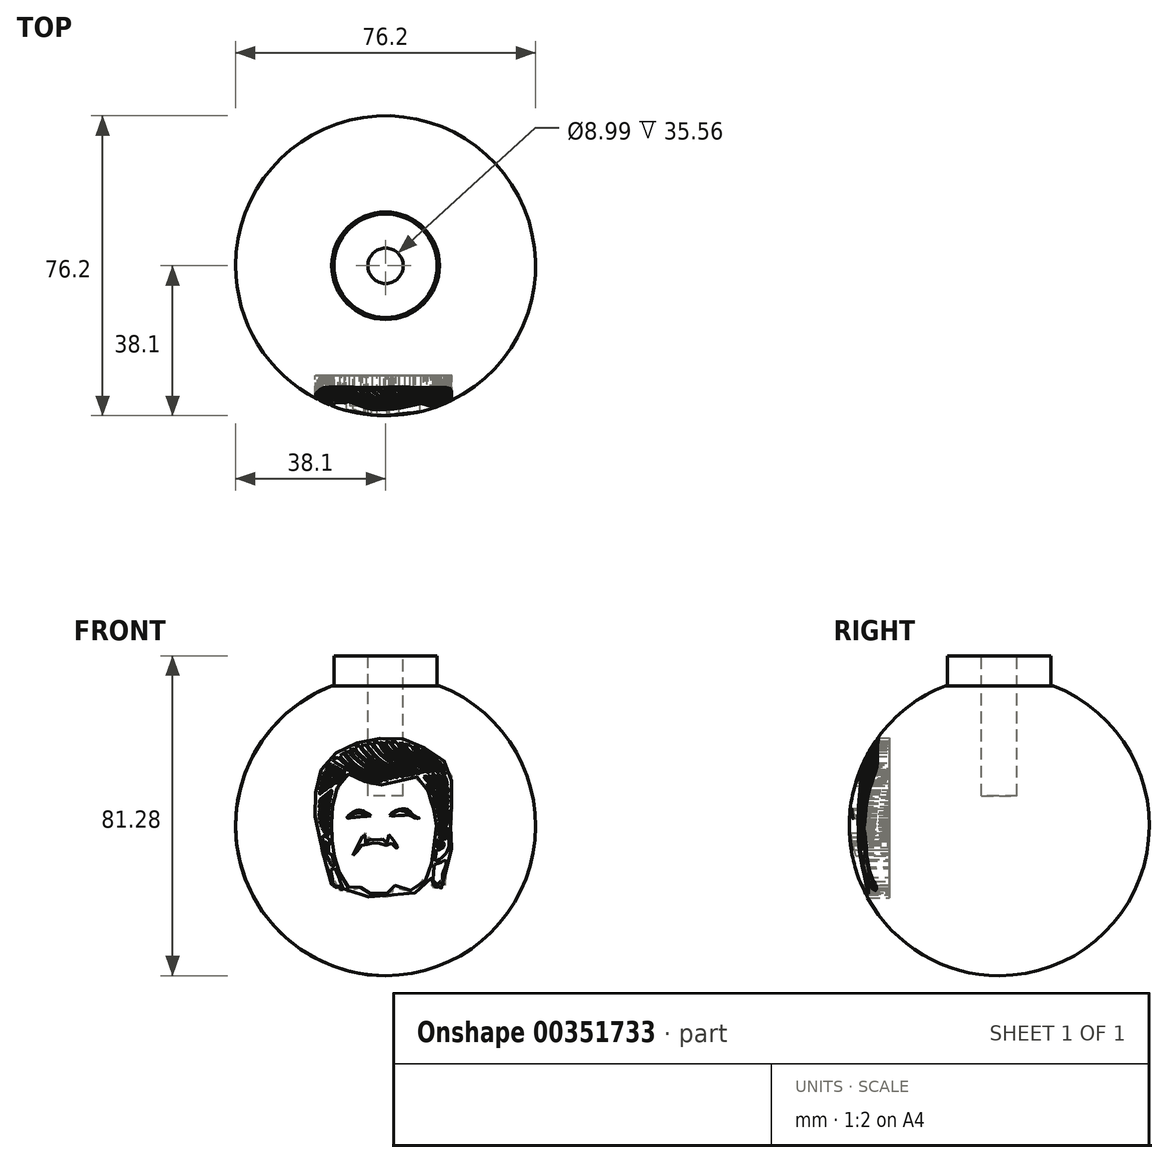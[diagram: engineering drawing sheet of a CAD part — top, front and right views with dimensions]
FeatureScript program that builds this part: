
annotation { "Feature Type Name" : "Feature", "Feature Type Description" : "" }
export const myFeature = defineFeature(function(context is Context, id is Id, definition is map)
    precondition{}
    {
        {
            var Q0;
            Q0=qCreatedBy(makeId("Front.planeOp"),FACE);
            var sketch = newSketch(context, id + "F0", { "sketchPlane" : qUnion([Q0])});
            skArc(sketch, "E0", {"start": v(0, 38.1) * mm, "mid": v(-38.1, 0) * mm, "end": v(0, -38.1) * mm});
            skLineSegment(sketch, "E1", {"start": v(0, 38.1) * mm, "end": v(0, -38.1) * mm});
            skSolve(sketch);
        }
        {
            var Q0;
            Q0=makeQuery(id+"F0.imprint","IMPRINT",FACE,{"disambiguationData":[TD([[makeQuery(id+"F0.imprint","IMPRINT",EDGE,{"derivedFrom":sQuery(id+"F0.wireOp",EDGE,"E0")}),1.0]])]});
            var Q1;
            Q1=sQuery(id+"F0.wireOp",EDGE,"E0");
            var Q2;
            Q2=sQuery(id+"F0.wireOp",EDGE,"E1");
            revolve(context, id + "F1", {"entities" : qUnion([Q0]), "surfaceEntities" : qUnion([Q1]), "axis" : qUnion([Q2]), "revolveType" : RevolveType.FULL});
        }
        {
            var Q0;
            Q0=qCreatedBy(makeId("Top.planeOp"),FACE);
            cPlane(context, id + "F2", {"entities" : qUnion([Q0]), "cplaneType" : CPlaneType.OFFSET, "offset" : 35.56 * mm, "width" : 152.4 * mm, "height" : 152.4 * mm});
        }
        {
            var Q0;
            Q0=qCreatedBy(id+"F2.planeOp",FACE);
            var sketch = newSketch(context, id + "F3", { "sketchPlane" : qUnion([Q0])});
            skLineSegment(sketch, "E2.bottom", {"start": v(16.51, 16.51) * mm, "end": v(-16.51, 16.51) * mm});
            skLineSegment(sketch, "E2.top", {"start": v(16.51, -16.51) * mm, "end": v(-16.51, -16.51) * mm});
            skLineSegment(sketch, "E2.left", {"start": v(16.51, 16.51) * mm, "end": v(16.51, -16.51) * mm});
            skLineSegment(sketch, "E2.right", {"start": v(-16.51, 16.51) * mm, "end": v(-16.51, -16.51) * mm});
            skPoint(sketch, "E2.middle", {"position": v(0, 0) * mm});
            skSolve(sketch);
        }
        {
            var Q0;
            Q0=makeQuery(id+"F3.imprint","IMPRINT",FACE,{"disambiguationData":[TD([[makeQuery(id+"F3.imprint","IMPRINT",EDGE,{"derivedFrom":sQuery(id+"F3.wireOp",EDGE,"E2.bottom")}),1.0]])]});
            extrude(context, id + "F4", {"entities" : qUnion([Q0]), "operationType" : NewBodyOperationType.REMOVE, "depth" : 25.4 * mm});
        }
        {
            var Q0;
            Q0=qCreatedBy(makeId("Front.planeOp"),FACE);
            cPlane(context, id + "F5", {"entities" : qUnion([Q0]), "cplaneType" : CPlaneType.OFFSET, "offset" : 40.64 * mm, "width" : 152.4 * mm, "height" : 152.4 * mm});
        }
        {
            var Q0;
            Q0=qCreatedBy(id+"F5.planeOp",FACE);
            var sketch = newSketch(context, id + "F6", { "sketchPlane" : qUnion([Q0])});
            skFitSpline(sketch, "E3", {"points": [v(-13.42, 4.94) * mm, v(-13.77, 1.48) * mm, v(-13.69, -2.98) * mm, v(-12.93, -8.07) * mm, v(-10.73, -14.01) * mm, v(-8.94, -16.04) * mm, v(-7.44, -16.48) * mm, v(-6.43, -16.38) * mm, v(-6.53, -16.1) * mm, v(-6.53, -15.75) * mm, v(-6.33, -15.56) * mm, v(-6.1, -15.27) * mm, v(-5.85, -15.13) * mm, v(-5.9, -15.51) * mm, v(-6.04, -15.75) * mm, v(-6.04, -16.04) * mm, v(-5.9, -16.38) * mm, v(-5.7, -16.62) * mm, v(-4.17, -17.17) * mm, v(-3.17, -17.46) * mm, v(-1.74, -17.5) * mm, v(0.28, -17.23) * mm, v(1.86, -16.73) * mm, v(2.44, -16.33) * mm, v(2.69, -15.98) * mm, v(2.14, -15.38) * mm, v(1.9, -15.13) * mm, v(1.9, -15.09) * mm, v(2.03, -15.13) * mm, v(2.29, -15.16) * mm, v(2.64, -15.3) * mm, v(2.9, -15.65) * mm, v(3.03, -16.11) * mm, v(3.36, -16.11) * mm, v(3.95, -16.24) * mm, v(4.51, -16.34) * mm, v(5.17, -16.44) * mm, v(5.99, -16.5) * mm, v(8.28, -15.87) * mm, v(11.23, -11.44) * mm, v(12.37, -4.65) * mm, v(12.9, 0) * mm, v(10.78, 8.79) * mm, v(8.61, 12.24) * mm, v(7.1, 12.14) * mm, v(-0.99, 10.36) * mm, v(-1.74, 10.17) * mm, v(-3.25, 10.26) * mm, v(-9.18, 13.18) * mm, v(-9.74, 12.43) * mm, v(-11.15, 10.54) * mm, v(-12.1, 9.98) * mm, v(-13.42, 4.94) * mm]});
            skFitSpline(sketch, "E4", {"points": [v(-16.44, 14.23) * mm, v(-15.15, 16.37) * mm, v(-10.88, 19.62) * mm, v(-5.66, 21.5) * mm, v(1.82, 22.36) * mm, v(7.43, 21.07) * mm, v(14.77, 16.6) * mm, v(16.5, 14.16) * mm, v(16.78, 11.72) * mm, v(16.78, 5.82) * mm, v(16.64, 0) * mm, v(16.45, 0) * mm, v(16.55, -1.09) * mm, v(16.86, -5.2) * mm, v(16.04, -7.5) * mm, v(15.94, -8.77) * mm, v(15.64, -10.4) * mm, v(15.19, -12.44) * mm, v(15.33, -14.6) * mm, v(15.33, -15.53) * mm, v(14.8, -16.07) * mm, v(13.82, -15.82) * mm, v(13.86, -16.43) * mm, v(12.35, -15.82) * mm, v(11.4, -15) * mm, v(11.59, -13.12) * mm, v(10.4, -14.85) * mm, v(6.34, -17.33) * mm, v(3.46, -17.05) * mm, v(2.34, -17.15) * mm, v(0.83, -18.05) * mm, v(-2.12, -18.34) * mm, v(-4.5, -17.98) * mm, v(-5.8, -17.11) * mm, v(-6.76, -17.17) * mm, v(-8.1, -17.26) * mm, v(-10.36, -16.11) * mm, v(-10.1, -17) * mm, v(-11.45, -16.63) * mm, v(-13.57, -15.24) * mm, v(-14.3, -10.82) * mm, v(-14.67, -10.07) * mm, v(-15.84, -8.34) * mm, v(-16.3, -6.15) * mm, v(-16.8, -1.78) * mm, v(-16.96, -0.91) * mm, v(-17.72, 1.07) * mm, v(-17.82, 3.82) * mm, v(-17.57, 6.16) * mm, v(-17.26, 6.77) * mm, v(-17.62, 7.48) * mm, v(-17.35, 11.15) * mm, v(-16.44, 14.23) * mm]});
            skFitSpline(sketch, "E5", {"points": [v(-16.9, 7.74) * mm, v(-16.92, 9.4) * mm, v(-16.35, 11.89) * mm, v(-15.38, 14.34) * mm, v(-14.2, 16.09) * mm, v(-13.85, 15.83) * mm, v(-13.44, 15.63) * mm, v(-9.88, 13.7) * mm, v(-9.85, 13.55) * mm, v(-9.94, 13.25) * mm, v(-9.96, 13.07) * mm, v(-10.02, 12.86) * mm, v(-10.1, 12.72) * mm, v(-10.26, 12.56) * mm, v(-10.4, 12.35) * mm, v(-11.15, 11.44) * mm, v(-11.38, 11.08) * mm, v(-12.27, 10.73) * mm, v(-12.68, 10.65) * mm, v(-13.14, 10.5) * mm, v(-13.39, 10.27) * mm, v(-13.8, 10.01) * mm, v(-15, 9.18) * mm, v(-16.54, 7.9) * mm, v(-16.71, 7.77) * mm, v(-16.9, 7.74) * mm]});
            skFitSpline(sketch, "E6", {"points": [v(-13.42, 9.18) * mm, v(-13.42, 8.8) * mm, v(-13.42, 8.66) * mm, v(-13.62, 7.7) * mm, v(-13.8, 6.07) * mm, v(-13.94, 4.94) * mm, v(-14.2, 2.5) * mm, v(-14.2, 0.72) * mm, v(-14.2, -2.59) * mm, v(-14.2, -2.74) * mm, v(-14.45, -2.56) * mm, v(-15.6, -1.9) * mm, v(-16.1, -1.17) * mm, v(-16.54, 0) * mm, v(-16.99, 1.6) * mm, v(-17.12, 3.67) * mm, v(-16.96, 5.93) * mm, v(-16.79, 6.52) * mm, v(-13.8, 9.18) * mm, v(-13.39, 9.38) * mm, v(-13.42, 9.18) * mm]});
            skFitSpline(sketch, "E7", {"points": [v(-13.8, -11.08) * mm, v(-13.6, -12.82) * mm, v(-13.42, -14.46) * mm, v(-13.05, -15.35) * mm, v(-12.64, -15.75) * mm, v(-12.36, -15.64) * mm, v(-12.1, -15.36) * mm, v(-11.92, -15.21) * mm, v(-11.45, -15.75) * mm, v(-11.45, -16.16) * mm, v(-11.15, -16.16) * mm, v(-10.8, -16.27) * mm, v(-10.82, -15.75) * mm, v(-11.15, -15.16) * mm, v(-11.89, -12.97) * mm, v(-12.38, -11.86) * mm, v(-12.85, -10.98) * mm, v(-13.23, -10.9) * mm, v(-13.39, -10.96) * mm, v(-13.8, -11.08) * mm]});
            skFitSpline(sketch, "E8", {"points": [v(-13.16, -10.5) * mm, v(-13.8, -9.94) * mm, v(-14.2, -9.49) * mm, v(-14.2, -9.05) * mm, v(-15, -7.55) * mm, v(-15, -5.02) * mm, v(-15, -4) * mm, v(-15.18, -4.12) * mm, v(-15.42, -4.98) * mm, v(-15.58, -6.15) * mm, v(-15.7, -5.07) * mm, v(-15.78, -4.1) * mm, v(-15.96, -2.43) * mm, v(-15.26, -2.64) * mm, v(-15, -2.98) * mm, v(-14.2, -3.34) * mm, v(-14.27, -3.64) * mm, v(-14.38, -4.38) * mm, v(-14.5, -5.67) * mm, v(-14.54, -6.55) * mm, v(-14.37, -7.35) * mm, v(-14.07, -7.15) * mm, v(-13.8, -6.9) * mm, v(-13.39, -8.16) * mm, v(-13.06, -9.97) * mm, v(-13.16, -10.5) * mm]});
            skFitSpline(sketch, "E9", {"points": [v(13.42, -6.15) * mm, v(12.99, -6.15) * mm, v(12.86, -6.8) * mm, v(12.82, -7.61) * mm, v(12.56, -8.85) * mm, v(12.77, -8.94) * mm, v(13.12, -8.85) * mm, v(14.19, -8.21) * mm, v(15.77, -6.15) * mm, v(16.15, -3.3) * mm, v(16.07, -2.82) * mm, v(15.43, -3.22) * mm, v(14.59, -3.52) * mm, v(14.04, -3.4) * mm, v(14.47, -3.88) * mm, v(14.77, -4.46) * mm, v(14.89, -5.2) * mm, v(14.28, -5.6) * mm, v(13.42, -6.15) * mm]});
            skFitSpline(sketch, "E10", {"points": [v(13.17, -3.55) * mm, v(13.14, -4.25) * mm, v(13.07, -5.2) * mm, v(13.1, -5.52) * mm, v(14.01, -4.88) * mm, v(14.13, -4.52) * mm, v(13.17, -3.55) * mm]});
            skFitSpline(sketch, "E11", {"points": [v(15.68, -0.47) * mm, v(15.37, -0.58) * mm, v(14.33, -1.18) * mm, v(13.64, -1.54) * mm, v(13.86, -1.63) * mm, v(14.42, -1.64) * mm, v(15.05, -1.52) * mm, v(15.75, -1.14) * mm, v(15.82, -0.65) * mm, v(15.68, -0.47) * mm]});
            skFitSpline(sketch, "E12", {"points": [v(13.28, -1.9) * mm, v(13.48, -2.43) * mm, v(14.02, -2.43) * mm, v(14.7, -2.38) * mm, v(15.2, -2.22) * mm, v(15.73, -1.91) * mm, v(16, -1.79) * mm, v(15.96, -1.4) * mm, v(15.87, -1.4) * mm, v(15.2, -1.84) * mm, v(14.61, -1.95) * mm, v(13.9, -1.91) * mm, v(13.28, -1.9) * mm]});
            skFitSpline(sketch, "E13", {"points": [v(13.54, -2.76) * mm, v(13.8, -3.08) * mm, v(14.04, -3.17) * mm, v(14.56, -3.15) * mm, v(15.06, -3.01) * mm, v(15.53, -2.83) * mm, v(15.87, -2.7) * mm, v(16.05, -2.52) * mm, v(16.02, -2.13) * mm, v(15.9, -2.16) * mm, v(15.59, -2.36) * mm, v(15.06, -2.6) * mm, v(14.7, -2.72) * mm, v(14.06, -2.76) * mm, v(13.54, -2.76) * mm]});
            skFitSpline(sketch, "E14", {"points": [v(-4.92, -10.15) * mm, v(-4.48, -10.38) * mm, v(-3.3, -10.82) * mm, v(-3.46, -10.96) * mm, v(-4.93, -11.44) * mm, v(-5.88, -12) * mm, v(-5.34, -11.95) * mm, v(-4.06, -11.53) * mm, v(-3.04, -11.25) * mm, v(-1.97, -11.1) * mm, v(-0.26, -11.1) * mm, v(0.76, -11.26) * mm, v(2.88, -11.68) * mm, v(3.83, -11.89) * mm, v(1.06, -10.7) * mm, v(0.14, -10.55) * mm, v(0.44, -10.34) * mm, v(0.9, -9.7) * mm, v(0.6, -9.81) * mm, v(-0.38, -10.1) * mm, v(-3.12, -10.27) * mm, v(-4.92, -10.15) * mm]});
            skFitSpline(sketch, "E15", {"points": [v(-4.97, -8.6) * mm, v(-3.92, -7.6) * mm, v(-3.47, -7.35) * mm, v(-3.1, -7.43) * mm, v(-2.85, -7.6) * mm, v(-2.12, -7.67) * mm, v(-1.56, -7.6) * mm, v(-1.22, -7.52) * mm, v(-0.93, -7.24) * mm, v(-0.75, -7.2) * mm, v(0, -7.6) * mm, v(0.43, -7.82) * mm, v(1.22, -8.35) * mm, v(0.19, -8.23) * mm, v(-0.93, -8.14) * mm, v(-3.29, -8.17) * mm, v(-4.65, -8.56) * mm, v(-4.97, -8.6) * mm]});
            skFitSpline(sketch, "E16", {"points": [v(-7.37, -10.48) * mm, v(-5.48, -8.8) * mm, v(-5.21, -8.67) * mm, v(-5.21, -8.4) * mm, v(-4.35, -7.64) * mm, v(-3.82, -7.17) * mm, v(-3.15, -7.06) * mm, v(-2.64, -7.33) * mm, v(-1.88, -7.3) * mm, v(-1.23, -7.08) * mm, v(-0.6, -6.91) * mm, v(0.6, -7.55) * mm, v(2, -8.6) * mm, v(2.8, -8.9) * mm, v(3.3, -9.12) * mm, v(3.52, -9.26) * mm, v(4.29, -10.53) * mm, v(3.8, -10.12) * mm, v(2.8, -9.4) * mm, v(1.75, -9.13) * mm, v(0.5, -8.9) * mm, v(-0.84, -8.74) * mm, v(-1.22, -8.67) * mm, v(-3.26, -8.7) * mm, v(-5.15, -9.24) * mm, v(-7, -10.33) * mm, v(-7.37, -10.48) * mm]});
            skFitSpline(sketch, "E17", {"points": [v(-8.24, -7.51) * mm, v(-5.15, -1.79) * mm, v(-5.36, -2.76) * mm, v(-5.4, -3.28) * mm, v(-5.03, -4.28) * mm, v(-4.45, -4.65) * mm, v(-4.48, -3.97) * mm, v(-4.42, -3.16) * mm, v(-4.4, -2.85) * mm, v(-3.7, -3.4) * mm, v(-3.06, -3.8) * mm, v(-2.12, -3.64) * mm, v(-1.13, -2.98) * mm, v(-0.34, -3.97) * mm, v(0, -4.65) * mm, v(0.63, -3.97) * mm, v(0.78, -2.88) * mm, v(0.48, -2.13) * mm, v(0.42, -1.79) * mm, v(3.41, -6.15) * mm, v(1.11, -4.28) * mm, v(0.96, -4.65) * mm, v(0, -4.94) * mm, v(-0.34, -4.65) * mm, v(-2.12, -4.37) * mm, v(-2.12, -4.22) * mm, v(-3.29, -4.34) * mm, v(-4.06, -4.88) * mm, v(-4.51, -4.88) * mm, v(-5.27, -4.34) * mm, v(-7.72, -7.21) * mm, v(-8.24, -7.51) * mm]});
            skFitSpline(sketch, "E18", {"points": [v(-13.49, 16.72) * mm, v(-7.3, 13.04) * mm, v(-4.42, 11.6) * mm, v(-2.35, 10.89) * mm, v(-1.73, 10.98) * mm, v(-1.45, 11.08) * mm, v(-2.26, 11.26) * mm, v(-3.32, 11.7) * mm, v(-7.28, 13.54) * mm, v(-10.87, 16.16) * mm, v(-12.15, 17.57) * mm, v(-12.19, 17.54) * mm, v(-13.17, 17) * mm, v(-13.49, 16.72) * mm]});
            skFitSpline(sketch, "E19", {"points": [v(-11.6, 17.91) * mm, v(-11.17, 17.23) * mm, v(-9.23, 15.39) * mm, v(-6.3, 13.48) * mm, v(-3.15, 12.03) * mm, v(-1.41, 11.42) * mm, v(-1.1, 11.3) * mm, v(-0.36, 11.34) * mm, v(-1.17, 11.61) * mm, v(-2.9, 12.3) * mm, v(-5.19, 13.48) * mm, v(-9.13, 16.4) * mm, v(-10.78, 18.55) * mm, v(-10.9, 18.52) * mm, v(-11.36, 18.18) * mm, v(-11.6, 17.91) * mm]});
            skFitSpline(sketch, "E20", {"points": [v(-10.36, 18.74) * mm, v(-9.94, 18.08) * mm, v(-8.47, 16.27) * mm, v(-5.8, 14.26) * mm, v(-2.2, 12.32) * mm, v(0, 11.56) * mm, v(0.62, 11.5) * mm, v(0.86, 11.69) * mm, v(0, 12.06) * mm, v(-1.07, 12.52) * mm, v(-4.28, 14.33) * mm, v(-7.1, 16.4) * mm, v(-9.57, 19.04) * mm, v(-9.6, 19.14) * mm, v(-9.82, 19.11) * mm, v(-10.36, 18.74) * mm]});
            skFitSpline(sketch, "E21", {"points": [v(-9.17, 19.38) * mm, v(-8.87, 19.04) * mm, v(-8.27, 18.06) * mm, v(-3.65, 14.33) * mm, v(-1.64, 13.2) * mm, v(0.55, 12.12) * mm, v(1.46, 11.93) * mm, v(2.15, 11.96) * mm, v(0.83, 12.62) * mm, v(-0.77, 13.5) * mm, v(-5.19, 16.47) * mm, v(-8.16, 19.46) * mm, v(-8.3, 19.76) * mm, v(-9.17, 19.38) * mm]});
            skFitSpline(sketch, "E22", {"points": [v(-7.8, 19.96) * mm, v(-6.32, 17.98) * mm, v(-3.4, 15.64) * mm, v(-0.35, 13.7) * mm, v(2.59, 12.12) * mm, v(2.75, 12.18) * mm, v(3.52, 12.29) * mm, v(2.64, 12.78) * mm, v(1.46, 13.33) * mm, v(-1.1, 14.9) * mm, v(-4, 17.07) * mm, v(-6.34, 19.76) * mm, v(-6.73, 20.42) * mm, v(-6.98, 20.34) * mm, v(-7.8, 19.96) * mm]});
            skFitSpline(sketch, "E23", {"points": [v(-6.18, 20.42) * mm, v(-4.91, 18.58) * mm, v(-2.85, 16.6) * mm, v(-0.63, 15.07) * mm, v(1.02, 14.02) * mm, v(2.94, 13.03) * mm, v(4.13, 12.4) * mm, v(4.98, 12.48) * mm, v(4.76, 12.65) * mm, v(2.34, 13.94) * mm, v(0.22, 15.29) * mm, v(-0.93, 16.08) * mm, v(-3.16, 17.98) * mm, v(-5.27, 20.73) * mm, v(-5.55, 20.75) * mm, v(-6.18, 20.42) * mm]});
            skFitSpline(sketch, "E24", {"points": [v(-4.85, 20.84) * mm, v(-3.87, 19.39) * mm, v(-2.05, 17.36) * mm, v(0.26, 15.67) * mm, v(3.8, 13.57) * mm, v(5.33, 12.63) * mm, v(6.22, 12.81) * mm, v(5.6, 13.23) * mm, v(1.3, 15.98) * mm, v(-1.74, 18.48) * mm, v(-3.82, 21) * mm, v(-4.28, 21) * mm, v(-4.85, 20.84) * mm]});
            skFitSpline(sketch, "E25", {"points": [v(-3.24, 21.2) * mm, v(-2.62, 20.1) * mm, v(-0.93, 18.14) * mm, v(0.78, 16.82) * mm, v(3.2, 15.08) * mm, v(6.32, 13.13) * mm, v(6.7, 12.81) * mm, v(7.64, 13.15) * mm, v(6.97, 13.54) * mm, v(4.47, 15.13) * mm, v(0.81, 17.73) * mm, v(-0.88, 19.55) * mm, v(-1.97, 21.23) * mm, v(-2.18, 21.23) * mm, v(-3.24, 21.2) * mm]});
            skFitSpline(sketch, "E26", {"points": [v(-1.42, 21.34) * mm, v(-0.41, 19.47) * mm, v(1.67, 17.6) * mm, v(6.22, 14.33) * mm, v(8.22, 13.18) * mm, v(8.97, 13.33) * mm, v(7.85, 14.06) * mm, v(4.5, 16.35) * mm, v(4.11, 16.58) * mm, v(2.37, 17.88) * mm, v(0.34, 19.6) * mm, v(-0.75, 21.34) * mm, v(-0.96, 21.34) * mm, v(-1.42, 21.34) * mm]});
            skFitSpline(sketch, "E27", {"points": [v(0, 21.44) * mm, v(0.61, 20) * mm, v(2.73, 18.06) * mm, v(5.16, 16.43) * mm, v(7.1, 15.03) * mm, v(9.03, 13.66) * mm, v(10.14, 13.48) * mm, v(9, 14.54) * mm, v(5.7, 16.71) * mm, v(2.13, 19.5) * mm, v(0.8, 21.44) * mm, v(0.43, 21.5) * mm, v(0, 21.44) * mm]});
            skFitSpline(sketch, "E28", {"points": [v(1.41, 21.29) * mm, v(1.88, 20.46) * mm, v(3.6, 18.68) * mm, v(5.52, 17.33) * mm, v(8.2, 15.52) * mm, v(10.04, 14.06) * mm, v(10.6, 13.53) * mm, v(11.51, 13.56) * mm, v(10.8, 14.33) * mm, v(9, 15.42) * mm, v(6.32, 17.57) * mm, v(5.42, 17.95) * mm, v(3.71, 19.6) * mm, v(2.83, 21.18) * mm, v(1.41, 21.29) * mm]});
            skFitSpline(sketch, "E29", {"points": [v(3.48, 21.05) * mm, v(3.73, 20.35) * mm, v(5.32, 18.43) * mm, v(6.32, 17.83) * mm, v(6.9, 17.43) * mm, v(8.27, 16.43) * mm, v(10.02, 15.13) * mm, v(11.34, 14.33) * mm, v(11.8, 13.66) * mm, v(12.14, 13.6) * mm, v(12.6, 13.7) * mm, v(12.13, 14.33) * mm, v(10.5, 15.46) * mm, v(7.85, 17.22) * mm, v(5.39, 19.28) * mm, v(4.72, 20.13) * mm, v(4.47, 20.9) * mm, v(4.23, 20.99) * mm, v(3.48, 21.05) * mm]});
            skFitSpline(sketch, "E30", {"points": [v(4.95, 20.74) * mm, v(5.1, 20.17) * mm, v(7.19, 18.18) * mm, v(9.46, 16.56) * mm, v(10.9, 15.56) * mm, v(12.2, 14.54) * mm, v(13, 13.61) * mm, v(13.8, 13.6) * mm, v(13.43, 14.33) * mm, v(12.1, 15.41) * mm, v(10.8, 16.4) * mm, v(9.46, 17.28) * mm, v(7.64, 18.77) * mm, v(6.72, 20.02) * mm, v(6.64, 20.32) * mm, v(6.32, 20.42) * mm, v(5.17, 20.7) * mm, v(4.95, 20.74) * mm]});
            skFitSpline(sketch, "E31", {"points": [v(7.15, 20.13) * mm, v(7.5, 19.38) * mm, v(9.17, 17.93) * mm, v(11.77, 16.05) * mm, v(13.23, 14.88) * mm, v(14.11, 13.83) * mm, v(14.14, 13.55) * mm, v(14.94, 13.13) * mm, v(15.45, 12.97) * mm, v(14.86, 13.84) * mm, v(13.57, 15.39) * mm, v(12.17, 16.52) * mm, v(9.87, 18.03) * mm, v(8.53, 19.27) * mm, v(8.43, 19.43) * mm, v(8.25, 19.84) * mm, v(7.64, 20.08) * mm, v(7.15, 20.13) * mm]});
            skFitSpline(sketch, "E32", {"points": [v(8.99, 19.38) * mm, v(9.6, 18.64) * mm, v(11.87, 17.01) * mm, v(13.05, 16.18) * mm, v(14.18, 15.17) * mm, v(15.23, 13.87) * mm, v(15.03, 14.33) * mm, v(13.8, 16.13) * mm, v(13.59, 16.35) * mm, v(12.13, 17.59) * mm, v(9.25, 19.42) * mm, v(8.99, 19.38) * mm]});
            skFitSpline(sketch, "E33", {"points": [v(12.47, -9.8) * mm, v(12.23, -11.4) * mm, v(12.02, -13.72) * mm, v(12.02, -14.64) * mm, v(12.35, -15.22) * mm, v(13.24, -15.82) * mm, v(13.26, -15.17) * mm, v(13.99, -14.13) * mm, v(14.23, -14.8) * mm, v(14.67, -15.15) * mm, v(14.6, -14.53) * mm, v(14.52, -12.18) * mm, v(15.16, -10.72) * mm, v(15.3, -8.64) * mm, v(14.87, -8.82) * mm, v(13.2, -9.6) * mm, v(12.47, -9.8) * mm]});
            skFitSpline(sketch, "E34", {"points": [v(9.63, 12.6) * mm, v(10.14, 11.77) * mm, v(11.67, 10.2) * mm, v(12.5, 8.86) * mm, v(14, 6.35) * mm, v(15.4, 4.53) * mm, v(15.87, 4.35) * mm, v(15.96, 4.57) * mm, v(15.87, 4.96) * mm, v(14.92, 6) * mm, v(13.96, 7.65) * mm, v(13.27, 9.12) * mm, v(11.93, 10.9) * mm, v(10.14, 12.72) * mm, v(9.63, 12.6) * mm]});
            skFitSpline(sketch, "E35", {"points": [v(10.8, 12.8) * mm, v(12.1, 11.5) * mm, v(13.44, 9.51) * mm, v(14.4, 7.65) * mm, v(15.3, 6.26) * mm, v(15.92, 5.57) * mm, v(16, 6.34) * mm, v(15.22, 7.12) * mm, v(14.44, 8.29) * mm, v(13.69, 10.06) * mm, v(12.4, 11.74) * mm, v(11.25, 12.72) * mm, v(10.8, 12.8) * mm]});
            skFitSpline(sketch, "E36", {"points": [v(11.67, 13.02) * mm, v(12.7, 11.94) * mm, v(13.67, 10.64) * mm, v(14.29, 9.51) * mm, v(14.92, 8.68) * mm, v(14.92, 8.53) * mm, v(14.92, 8.29) * mm, v(15.46, 7.54) * mm, v(15.95, 6.83) * mm, v(15.95, 7.03) * mm, v(15.76, 7.9) * mm, v(15.35, 8.6) * mm, v(13.33, 12.02) * mm, v(12.44, 13.02) * mm, v(12.1, 13) * mm, v(11.67, 13.02) * mm]});
            skFitSpline(sketch, "E37", {"points": [v(13.01, 13) * mm, v(13.67, 11.94) * mm, v(14.54, 10.68) * mm, v(15.42, 9) * mm, v(15.82, 8.36) * mm, v(15.86, 9.56) * mm, v(15.67, 9.73) * mm, v(15.1, 10.85) * mm, v(14.44, 11.96) * mm, v(13.6, 12.96) * mm, v(13.3, 13.02) * mm, v(13.01, 13) * mm]});
            skFitSpline(sketch, "E38", {"points": [v(14.16, 12.87) * mm, v(14.93, 11.7) * mm, v(15.65, 10.24) * mm, v(15.54, 11.4) * mm, v(15.16, 12.45) * mm, v(14.63, 12.72) * mm, v(14.16, 12.87) * mm]});
            skFitSpline(sketch, "E39", {"points": [v(10.57, 10.77) * mm, v(11.38, 8.7) * mm, v(11.59, 8.5) * mm, v(12.1, 7.96) * mm, v(12.59, 7.28) * mm, v(13.05, 6.32) * mm, v(13.84, 5.24) * mm, v(14.44, 4.43) * mm, v(15.48, 3.9) * mm, v(15.84, 3.94) * mm, v(15.48, 4.18) * mm, v(14.44, 5.4) * mm, v(13.25, 6.98) * mm, v(12.1, 8.79) * mm, v(11.2, 10.28) * mm, v(10.57, 10.77) * mm]});
            skFitSpline(sketch, "E40", {"points": [v(12.1, 7.28) * mm, v(12.55, 5.69) * mm, v(12.76, 4.82) * mm, v(13.47, 4.25) * mm, v(13.98, 3.72) * mm, v(14.31, 3.39) * mm, v(14.92, 2.95) * mm, v(15.88, 3) * mm, v(16.01, 3.11) * mm, v(15.84, 3.55) * mm, v(15.4, 3.65) * mm, v(14.92, 3.7) * mm, v(14.27, 4.23) * mm, v(13.53, 5.07) * mm, v(12.7, 6.46) * mm, v(12.43, 7.03) * mm, v(12.1, 7.45) * mm, v(12.1, 7.28) * mm]});
            skFitSpline(sketch, "E41", {"points": [v(12.86, 4.29) * mm, v(13.06, 3.5) * mm, v(13.43, 3.1) * mm, v(14.9, 2.08) * mm, v(16.04, 1.9) * mm, v(16, 2.59) * mm, v(15.84, 2.6) * mm, v(15.52, 2.6) * mm, v(14.78, 2.69) * mm, v(14.3, 3.1) * mm, v(13.05, 4.13) * mm, v(12.86, 4.29) * mm]});
            skFitSpline(sketch, "E42", {"points": [v(13.22, 2.85) * mm, v(13.4, 2.1) * mm, v(14.14, 1.78) * mm, v(14.98, 1.27) * mm, v(15.76, 1.04) * mm, v(16.1, 1) * mm, v(16.03, 1.56) * mm, v(15.44, 1.62) * mm, v(14.63, 1.95) * mm, v(13.66, 2.56) * mm, v(13.18, 3) * mm, v(13.22, 2.85) * mm]});
            skFitSpline(sketch, "E43", {"points": [v(13.36, 1.7) * mm, v(13.76, 1.1) * mm, v(14.44, 0.66) * mm, v(15.33, 0.15) * mm, v(15.55, 0.26) * mm, v(15.84, 0.67) * mm, v(15.7, 0.74) * mm, v(15.17, 0.9) * mm, v(14.44, 1.27) * mm, v(13.97, 1.62) * mm, v(13.55, 1.72) * mm, v(13.36, 1.7) * mm]});
            skFitSpline(sketch, "E44", {"points": [v(13.46, 0.86) * mm, v(13.46, 0.39) * mm, v(13.44, 0.26) * mm, v(14.12, -0.06) * mm, v(14.52, -0.36) * mm, v(14.73, -0.26) * mm, v(14.98, 0) * mm, v(14.44, 0.36) * mm, v(13.93, 0.69) * mm, v(13.46, 0.86) * mm]});
            skFitSpline(sketch, "E45", {"points": [v(13.41, -0.1) * mm, v(13.32, -1.04) * mm, v(14.27, -0.56) * mm, v(13.68, -0.13) * mm, v(13.41, -0.1) * mm]});
            skFitSpline(sketch, "E46", {"points": [v(-15.45, 13.66) * mm, v(-15.82, 13.03) * mm, v(-15.32, 13.32) * mm, v(-13.95, 14.06) * mm, v(-12.92, 15.09) * mm, v(-13.04, 15.26) * mm, v(-13.48, 15.41) * mm, v(-14.04, 14.76) * mm, v(-14.76, 14.06) * mm, v(-15.45, 13.66) * mm]});
            skFitSpline(sketch, "E47", {"points": [v(-15.12, 14.25) * mm, v(-13.88, 15.44) * mm, v(-13.88, 15.55) * mm, v(-14.13, 15.9) * mm, v(-14.34, 15.65) * mm, v(-15.12, 14.25) * mm]});
            skFitSpline(sketch, "E48", {"points": [v(-15.9, 12.57) * mm, v(-16.18, 11.68) * mm, v(-15.25, 12.15) * mm, v(-13.04, 13.52) * mm, v(-12.03, 14.61) * mm, v(-12.22, 14.83) * mm, v(-12.57, 14.95) * mm, v(-13.62, 13.88) * mm, v(-14.7, 13.18) * mm, v(-15.77, 12.72) * mm, v(-15.9, 12.57) * mm]});
            skFitSpline(sketch, "E49", {"points": [v(-16.4, 11.21) * mm, v(-16.63, 10.4) * mm, v(-15.9, 10.57) * mm, v(-14.19, 11.46) * mm, v(-12.18, 12.98) * mm, v(-11.16, 14.23) * mm, v(-11.2, 14.23) * mm, v(-11.65, 14.52) * mm, v(-12.08, 14.06) * mm, v(-15.53, 11.58) * mm, v(-16.14, 11.25) * mm, v(-16.4, 11.21) * mm]});
            skFitSpline(sketch, "E50", {"points": [v(-16.67, 9.99) * mm, v(-16.8, 9.15) * mm, v(-16, 9.29) * mm, v(-13.53, 10.73) * mm, v(-12.11, 11.94) * mm, v(-10.41, 13.48) * mm, v(-10.27, 13.66) * mm, v(-10.9, 14.06) * mm, v(-11.15, 13.66) * mm, v(-12.65, 12.2) * mm, v(-14.54, 10.92) * mm, v(-16.26, 10.11) * mm, v(-16.44, 10.11) * mm, v(-16.67, 9.99) * mm]});
            skFitSpline(sketch, "E51", {"points": [v(-16.8, 8.72) * mm, v(-16.78, 8) * mm, v(-16.17, 8.4) * mm, v(-15.47, 9.04) * mm, v(-13.97, 10.02) * mm, v(-13.5, 10.37) * mm, v(-13.14, 10.68) * mm, v(-12.34, 10.86) * mm, v(-11.62, 11.1) * mm, v(-10.95, 11.94) * mm, v(-10.16, 13.36) * mm, v(-11.3, 12.32) * mm, v(-13.14, 10.9) * mm, v(-14.16, 10.2) * mm, v(-16.21, 8.98) * mm, v(-16.64, 8.77) * mm, v(-16.8, 8.72) * mm]});
            skFitSpline(sketch, "E52", {"points": [v(-16.76, 5.8) * mm, v(-16.79, 6.33) * mm, v(-15.43, 7.62) * mm, v(-13.65, 9.04) * mm, v(-13.56, 8.7) * mm, v(-14.32, 8.29) * mm, v(-16.44, 6.24) * mm, v(-16.66, 6) * mm, v(-16.76, 5.8) * mm]});
            skFitSpline(sketch, "E53", {"points": [v(-16.85, 5.15) * mm, v(-15.76, 6.53) * mm, v(-14.09, 8.04) * mm, v(-13.68, 8.27) * mm, v(-13.76, 7.9) * mm, v(-13.86, 7.62) * mm, v(-14.23, 7.26) * mm, v(-15.74, 6) * mm, v(-16.79, 4.5) * mm, v(-16.85, 5.15) * mm]});
            skFitSpline(sketch, "E54", {"points": [v(-16.89, 3.92) * mm, v(-16.8, 3.5) * mm, v(-16.25, 4.38) * mm, v(-14.09, 6.4) * mm, v(-13.93, 7.07) * mm, v(-15.48, 5.8) * mm, v(-16.44, 4.45) * mm, v(-16.89, 3.92) * mm]});
            skFitSpline(sketch, "E55", {"points": [v(-16.85, 3.06) * mm, v(-16.87, 2.4) * mm, v(-16, 3.64) * mm, v(-14.44, 5.22) * mm, v(-14.14, 5.38) * mm, v(-14.05, 6) * mm, v(-14.46, 5.73) * mm, v(-15.69, 4.66) * mm, v(-16.85, 3.06) * mm]});
            skFitSpline(sketch, "E56", {"points": [v(-16.82, 2.1) * mm, v(-16.7, 1.46) * mm, v(-15.53, 3) * mm, v(-14.28, 4.05) * mm, v(-14.25, 4.93) * mm, v(-16.08, 3.17) * mm, v(-16.82, 2.1) * mm]});
            skFitSpline(sketch, "E57", {"points": [v(-16.65, 1.26) * mm, v(-16.53, 0.55) * mm, v(-16.06, 1.26) * mm, v(-15, 2.4) * mm, v(-14.43, 2.78) * mm, v(-14.27, 3.5) * mm, v(-14.8, 3.24) * mm, v(-15.7, 2.4) * mm, v(-16.44, 1.45) * mm, v(-16.65, 1.26) * mm]});
            skFitSpline(sketch, "E58", {"points": [v(-16.36, 0.24) * mm, v(-16.25, -0.29) * mm, v(-15.4, 0.99) * mm, v(-14.44, 1.67) * mm, v(-14.44, 2.4) * mm, v(-14.87, 2.16) * mm, v(-16.1, 0.68) * mm, v(-16.36, 0.24) * mm]});
            skFitSpline(sketch, "E59", {"points": [v(-16.12, -0.65) * mm, v(-15.95, -0.94) * mm, v(-15.15, 0.08) * mm, v(-14.5, 0.6) * mm, v(-14.46, 1.27) * mm, v(-14.65, 1.07) * mm, v(-15.35, 0.53) * mm, v(-15.98, -0.32) * mm, v(-16.12, -0.65) * mm]});
            skFitSpline(sketch, "E60", {"points": [v(-15.8, -1.2) * mm, v(-15.55, -1.65) * mm, v(-15.36, -1.08) * mm, v(-14.61, -0.41) * mm, v(-14.44, -0.29) * mm, v(-14.4, 0.22) * mm, v(-14.47, 0.35) * mm, v(-15, 0) * mm, v(-15.57, -0.78) * mm, v(-15.8, -1.2) * mm]});
            skFitSpline(sketch, "E61", {"points": [v(-15.36, -1.72) * mm, v(-14.96, -2.07) * mm, v(-14.49, -1.41) * mm, v(-14.36, -0.65) * mm, v(-15, -1.32) * mm, v(-15.36, -1.72) * mm]});
            skFitSpline(sketch, "E62", {"points": [v(-14.7, -2.18) * mm, v(-14.4, -2.37) * mm, v(-14.34, -1.78) * mm, v(-14.49, -1.94) * mm, v(-14.7, -2.18) * mm]});
            skFitSpline(sketch, "E63", {"points": [v(-8.4, 1.22) * mm, v(-8.4, 0.47) * mm, v(-7.41, 0.63) * mm, v(-5.53, 1.89) * mm, v(-5.47, 2.03) * mm, v(-6, 1.7) * mm, v(-7.6, 1.26) * mm, v(-8.4, 1.22) * mm]});
            skFitSpline(sketch, "E64", {"points": [v(-12.17, 1.87) * mm, v(-11.18, 1.83) * mm, v(-10.96, 2.37) * mm, v(-9.82, 3.7) * mm, v(-6.93, 4.2) * mm, v(-5.37, 3.4) * mm, v(-4.84, 3.4) * mm, v(-4.74, 4.38) * mm, v(-6.93, 4.93) * mm, v(-10.55, 4.6) * mm, v(-10.92, 4.68) * mm, v(-9, 5.15) * mm, v(-9.17, 5.4) * mm, v(-10.44, 6) * mm, v(-8.87, 5.6) * mm, v(-9.6, 6.52) * mm, v(-8.29, 5.75) * mm, v(-9.3, 7.02) * mm, v(-7.69, 6.23) * mm, v(-8.57, 7.32) * mm, v(-7.13, 6.52) * mm, v(-8.01, 7.58) * mm, v(-6.07, 6.52) * mm, v(-6.16, 6.86) * mm, v(-6.09, 7.97) * mm, v(-5.33, 6) * mm, v(-5.23, 8.29) * mm, v(-5.14, 7.85) * mm, v(-4.75, 6) * mm, v(-4.14, 6.28) * mm, v(-3.59, 7.34) * mm, v(-4.05, 5.21) * mm, v(-4.24, 3.94) * mm, v(-4.38, 2.85) * mm, v(-5.97, 2.85) * mm, v(-7.25, 2.64) * mm, v(-9.85, 2.6) * mm, v(-10.86, 1.77) * mm, v(-10.9, 1.27) * mm, v(-11.11, 0.89) * mm, v(-11.5, 0.52) * mm, v(-11.23, 1.1) * mm, v(-12.09, 1.1) * mm, v(-11.32, 1.51) * mm, v(-12.17, 1.87) * mm]});
            skSolve(sketch);
        }
        {
            var Q0;
            Q0=makeQuery(id+"F6.imprint","IMPRINT",FACE,{"disambiguationData":[TD([[makeQuery(id+"F6.imprint","IMPRINT",EDGE,{"derivedFrom":sQuery(id+"F6.wireOp",EDGE,"E3")}),-1.0]])]});
            var Q1;
            Q1=makeQuery(id+"F6.imprint","IMPRINT",FACE,{"disambiguationData":[TD([[makeQuery(id+"F6.imprint","IMPRINT",EDGE,{"derivedFrom":sQuery(id+"F6.wireOp",EDGE,"E5")}),-1.0]])]});
            var Q2;
            Q2=makeQuery(id+"F6.imprint","IMPRINT",FACE,{"disambiguationData":[TD([[makeQuery(id+"F6.imprint","IMPRINT",EDGE,{"derivedFrom":sQuery(id+"F6.wireOp",EDGE,"E6")}),-1.0]])]});
            var Q3;
            Q3=makeQuery(id+"F6.imprint","IMPRINT",FACE,{"disambiguationData":[TD([[makeQuery(id+"F6.imprint","IMPRINT",EDGE,{"derivedFrom":sQuery(id+"F6.wireOp",EDGE,"E17")}),-1.0]])]});
            extrude(context, id + "F7", {"entities" : qUnion([Q0, Q1, Q2, Q3]), "operationType" : NewBodyOperationType.REMOVE, "oppositeDirection" : true, "depth" : 12.7 * mm});
        }
        {
            var Q0;
            Q0=makeQuery(id+"F4.boolean.opBoolean","COPY",FACE,{"derivedFrom":makeQuery(id+"F4.opExtrude","CAP_FACE",FACE,{"disambiguationData":[OSD([sQuery(id+"F3.wireOp",EDGE,"E2.bottom"),sQuery(id+"F3.wireOp",EDGE,"E2.top"),sQuery(id+"F3.wireOp",EDGE,"E2.left"),sQuery(id+"F3.wireOp",EDGE,"E2.right")])],"isStart":true})});
            var sketch = newSketch(context, id + "F8", { "sketchPlane" : qUnion([Q0])});
            skCircle(sketch, "E65", {"center": v(0, 0) * mm, "radius": 13.14 * mm});
            skSolve(sketch);
        }
        {
            var Q0;
            Q0 = qSketchRegion(id + "F8", true);
            extrude(context, id + "F9", {"entities" : qUnion([Q0]), "operationType" : NewBodyOperationType.ADD, "depth" : 7.62 * mm});
        }
        {
            var Q0;
            Q0=makeQuery(id+"F9.opExtrude","CAP_FACE",FACE,{"disambiguationData":[OSD([sQuery(id+"F8.wireOp",EDGE,"E65")])],"isStart":false});
            var sketch = newSketch(context, id + "F10", { "sketchPlane" : qUnion([Q0])});
            skCircle(sketch, "E66", {"center": v(0, 0) * mm, "radius": 4.5 * mm});
            skSolve(sketch);
        }
        {
            var Q0;
            Q0=makeQuery(id+"F10.imprint","IMPRINT",FACE,{"disambiguationData":[TD([[makeQuery(id+"F10.imprint","IMPRINT",EDGE,{"derivedFrom":sQuery(id+"F10.wireOp",EDGE,"E66")}),1.0]])]});
            extrude(context, id + "F11", {"entities" : qUnion([Q0]), "operationType" : NewBodyOperationType.REMOVE, "oppositeDirection" : true, "depth" : 10.16 * mm});
        }
        {
            var Q0;
            Q0=makeQuery(id+"F11.boolean.opBoolean","COPY",FACE,{"derivedFrom":makeQuery(id+"F11.opExtrude","CAP_FACE",FACE,{"disambiguationData":[OSD([sQuery(id+"F10.wireOp",EDGE,"E66")])],"isStart":false})});
            extrude(context, id + "F12", {"entities" : qUnion([Q0]), "operationType" : NewBodyOperationType.REMOVE, "oppositeDirection" : true, "depth" : 25.4 * mm});
        }
        {
            var Q0;
            Q0=qCreatedBy(id+"F5.planeOp",FACE);
            var sketch = newSketch(context, id + "F13", { "sketchPlane" : qUnion([Q0])});
            skFitSpline(sketch, "E67", {"points": [v(0.96, 2.64) * mm, v(3.18, 4.07) * mm, v(5.88, 3.96) * mm, v(7.6, 2.24) * mm, v(8.73, 1.93) * mm, v(7.71, 1.85) * mm, v(6.78, 2.41) * mm, v(5.32, 2.7) * mm, v(1.27, 2.53) * mm, v(0.96, 2.64) * mm]});
            skFitSpline(sketch, "E68", {"points": [v(-3.63, 2.53) * mm, v(-4.98, 3.34) * mm, v(-7.18, 3.93) * mm, v(-9.88, 2.02) * mm, v(-8.81, 2.02) * mm, v(-3.94, 2.47) * mm, v(-3.63, 2.53) * mm]});
            skSolve(sketch);
        }
        {
            var Q0;
            Q0 = qSketchRegion(id + "F13", true);
            extrude(context, id + "F14", {"entities" : qUnion([Q0]), "operationType" : NewBodyOperationType.REMOVE, "oppositeDirection" : true, "depth" : 7.62 * mm});
        }
        {
            var Q0;
            Q0=makeQuery(id+"F7.boolean.opBoolean","COPY",FACE,{"derivedFrom":makeQuery(id+"F7.opExtrude","CAP_FACE",FACE,{"disambiguationData":[OSD([sQuery(id+"F6.wireOp",EDGE,"E3"),sQuery(id+"F6.wireOp",EDGE,"E4"),sQuery(id+"F6.wireOp",EDGE,"E7"),sQuery(id+"F6.wireOp",EDGE,"E8"),sQuery(id+"F6.wireOp",EDGE,"E9"),sQuery(id+"F6.wireOp",EDGE,"E10"),sQuery(id+"F6.wireOp",EDGE,"E11"),sQuery(id+"F6.wireOp",EDGE,"E12"),sQuery(id+"F6.wireOp",EDGE,"E13"),sQuery(id+"F6.wireOp",EDGE,"E18"),sQuery(id+"F6.wireOp",EDGE,"E19"),sQuery(id+"F6.wireOp",EDGE,"E20"),sQuery(id+"F6.wireOp",EDGE,"E21"),sQuery(id+"F6.wireOp",EDGE,"E22"),sQuery(id+"F6.wireOp",EDGE,"E23"),sQuery(id+"F6.wireOp",EDGE,"E24"),sQuery(id+"F6.wireOp",EDGE,"E25"),sQuery(id+"F6.wireOp",EDGE,"E26"),sQuery(id+"F6.wireOp",EDGE,"E27"),sQuery(id+"F6.wireOp",EDGE,"E28"),sQuery(id+"F6.wireOp",EDGE,"E29"),sQuery(id+"F6.wireOp",EDGE,"E30"),sQuery(id+"F6.wireOp",EDGE,"E31"),sQuery(id+"F6.wireOp",EDGE,"E32"),sQuery(id+"F6.wireOp",EDGE,"E33"),sQuery(id+"F6.wireOp",EDGE,"E34"),sQuery(id+"F6.wireOp",EDGE,"E35"),sQuery(id+"F6.wireOp",EDGE,"E36"),sQuery(id+"F6.wireOp",EDGE,"E37"),sQuery(id+"F6.wireOp",EDGE,"E38"),sQuery(id+"F6.wireOp",EDGE,"E39"),sQuery(id+"F6.wireOp",EDGE,"E40"),sQuery(id+"F6.wireOp",EDGE,"E41"),sQuery(id+"F6.wireOp",EDGE,"E42"),sQuery(id+"F6.wireOp",EDGE,"E43"),sQuery(id+"F6.wireOp",EDGE,"E44"),sQuery(id+"F6.wireOp",EDGE,"E45"),sQuery(id+"F6.wireOp",EDGE,"E46"),sQuery(id+"F6.wireOp",EDGE,"E47"),sQuery(id+"F6.wireOp",EDGE,"E48"),sQuery(id+"F6.wireOp",EDGE,"E49"),sQuery(id+"F6.wireOp",EDGE,"E50"),sQuery(id+"F6.wireOp",EDGE,"E51"),sQuery(id+"F6.wireOp",EDGE,"E52"),sQuery(id+"F6.wireOp",EDGE,"E53"),sQuery(id+"F6.wireOp",EDGE,"E54"),sQuery(id+"F6.wireOp",EDGE,"E55"),sQuery(id+"F6.wireOp",EDGE,"E56"),sQuery(id+"F6.wireOp",EDGE,"E57"),sQuery(id+"F6.wireOp",EDGE,"E58"),sQuery(id+"F6.wireOp",EDGE,"E59"),sQuery(id+"F6.wireOp",EDGE,"E60"),sQuery(id+"F6.wireOp",EDGE,"E61"),sQuery(id+"F6.wireOp",EDGE,"E62")])],"isStart":false})});
            var sketch = newSketch(context, id + "F15", { "sketchPlane" : qUnion([Q0])});
            skFitSpline(sketch, "E69", {"points": [v(-9.12, 2.45) * mm, v(-7.3, 3.22) * mm, v(-5.16, 2.84) * mm, v(-5.26, 3) * mm, v(-6.25, 3.53) * mm, v(-7.9, 3.5) * mm, v(-9.01, 2.78) * mm, v(-9.1, 2.63) * mm, v(-9.12, 2.45) * mm]});
            skFitSpline(sketch, "E70", {"points": [v(1.88, 3.03) * mm, v(3.22, 3.74) * mm, v(5, 3.6) * mm, v(6.28, 3) * mm, v(5.56, 3.71) * mm, v(3.78, 4.1) * mm, v(2.3, 3.55) * mm, v(1.92, 3.22) * mm, v(1.63, 2.9) * mm, v(1.88, 3.03) * mm]});
            skSolve(sketch);
        }
        {
            var Q0;
            Q0 = qSketchRegion(id + "F15", true);
            extrude(context, id + "F16", {"entities" : qUnion([Q0]), "operationType" : NewBodyOperationType.ADD, "depth" : 7.62 * mm});
        }
    });
